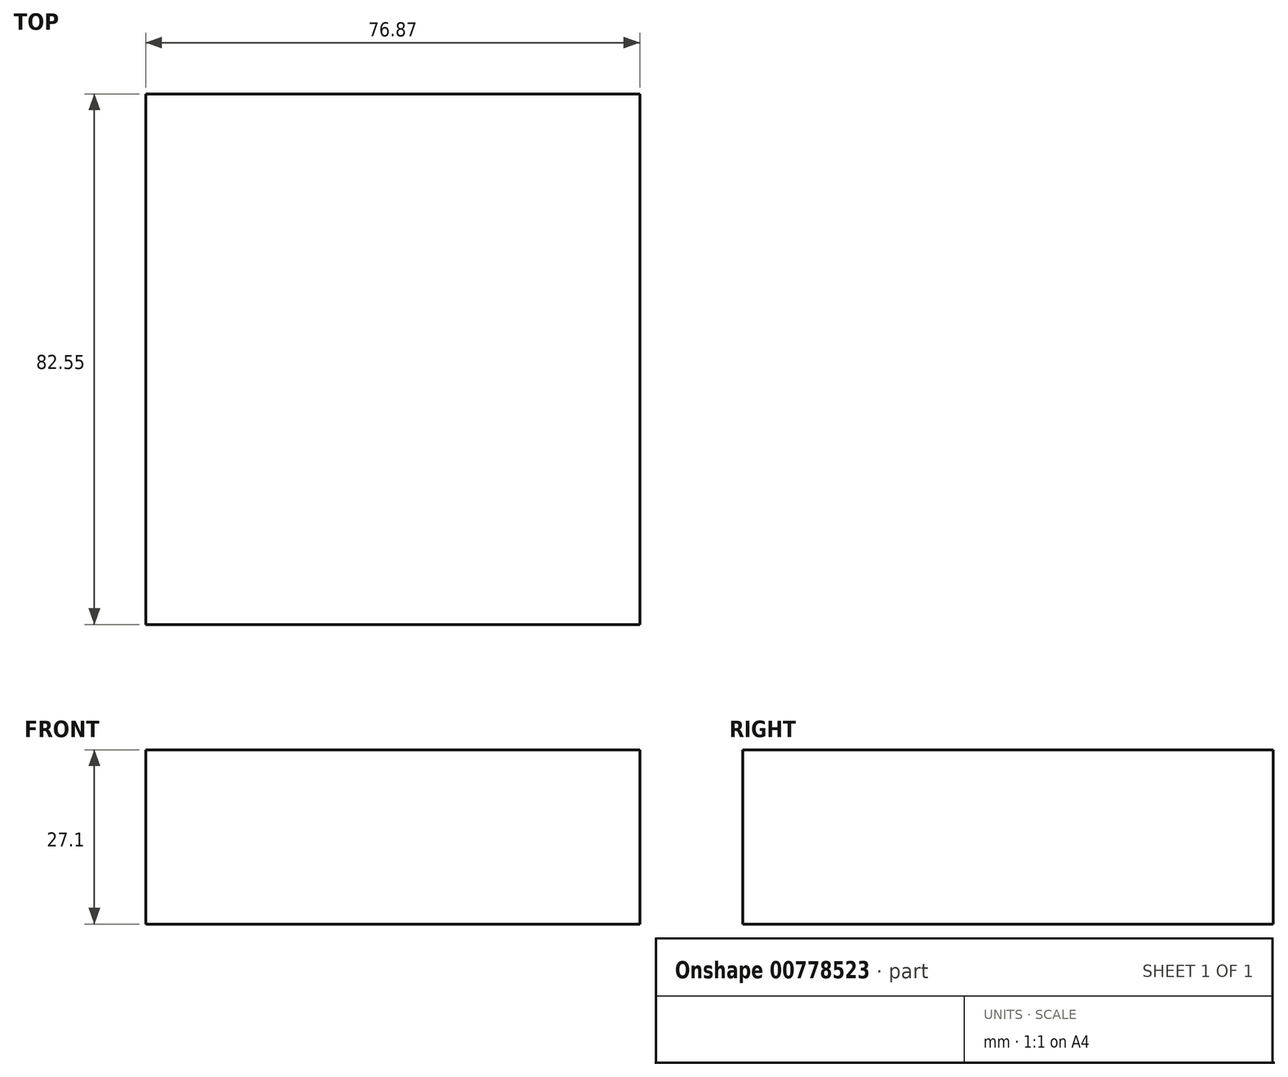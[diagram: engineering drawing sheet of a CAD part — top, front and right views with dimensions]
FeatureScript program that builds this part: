
annotation { "Feature Type Name" : "Feature", "Feature Type Description" : "" }
export const myFeature = defineFeature(function(context is Context, id is Id, definition is map)
    precondition{}
    {
        {
            var Q0;
            Q0=qCreatedBy(makeId("Front.planeOp"),FACE);
            var sketch = newSketch(context, id + "F0", { "sketchPlane" : qUnion([Q0])});
            skLineSegment(sketch, "E0.bottom", {"start": v(0, 0) * mm, "end": v(-76.87, 0) * mm});
            skLineSegment(sketch, "E0.top", {"start": v(0, 27.1) * mm, "end": v(-76.87, 27.1) * mm});
            skLineSegment(sketch, "E0.left", {"start": v(0, 0) * mm, "end": v(0, 27.1) * mm});
            skLineSegment(sketch, "E0.right", {"start": v(-76.87, 0) * mm, "end": v(-76.87, 27.1) * mm});
            skSolve(sketch);
        }
        {
            var Q0;
            Q0=makeQuery(id+"F0.imprint","IMPRINT",FACE,{"disambiguationData":[TD([[makeQuery(id+"F0.imprint","IMPRINT",EDGE,{"derivedFrom":sQuery(id+"F0.wireOp",EDGE,"E0.bottom")}),-1.0]])]});
            extrude(context, id + "F1", {"entities" : qUnion([Q0]), "depth" : 82.55 * mm, "offsetDistance" : 25.4 * mm});
        }
    });
